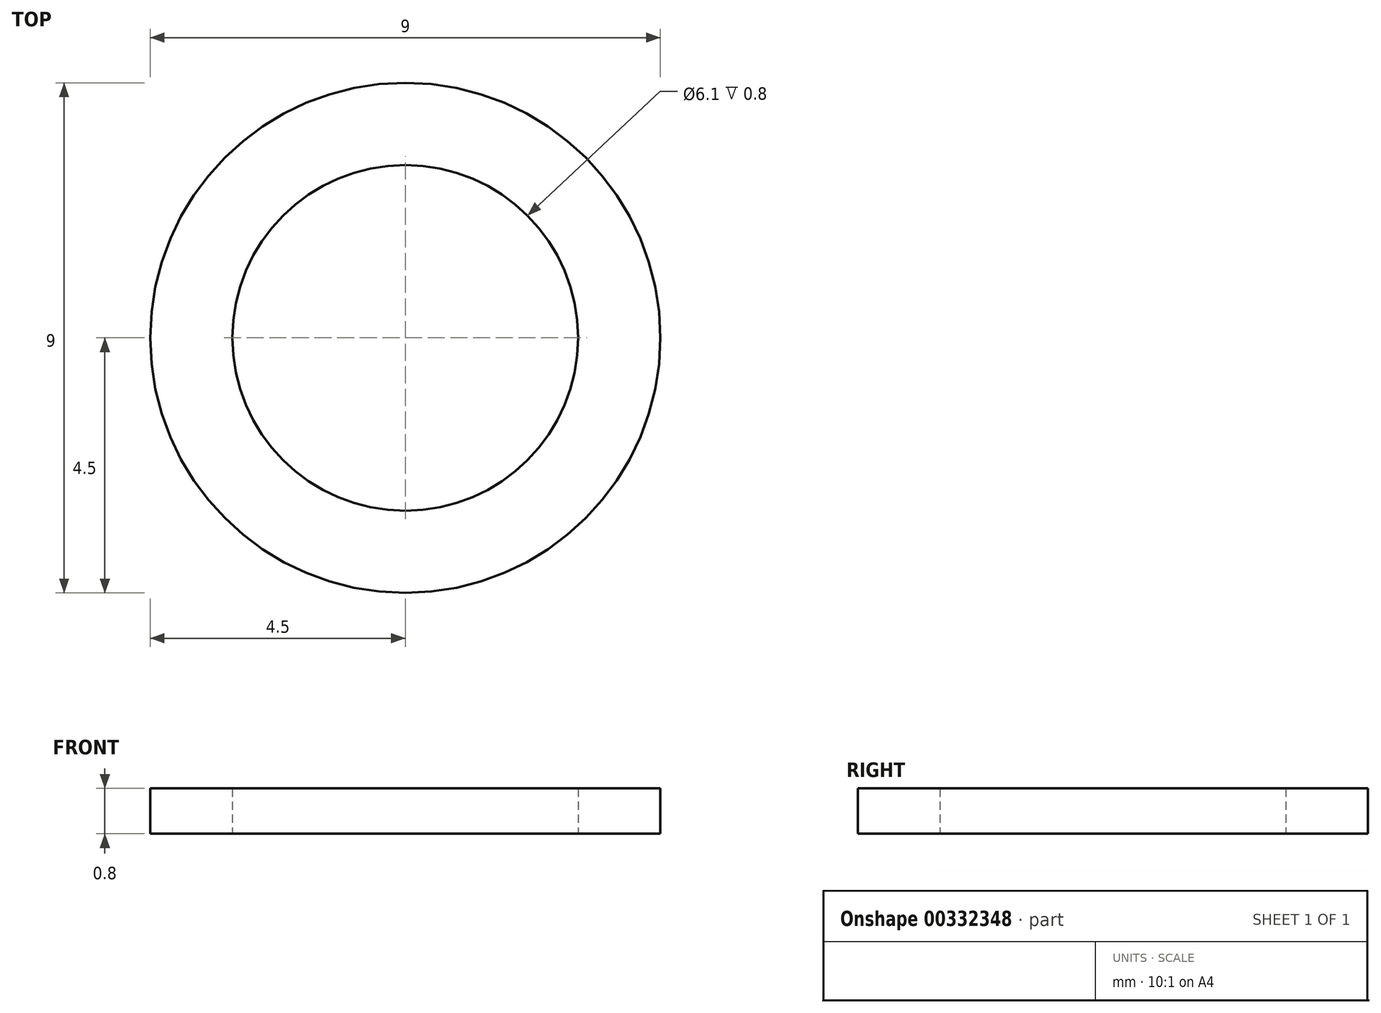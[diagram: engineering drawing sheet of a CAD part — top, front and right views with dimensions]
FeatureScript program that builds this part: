
annotation { "Feature Type Name" : "Feature", "Feature Type Description" : "" }
export const myFeature = defineFeature(function(context is Context, id is Id, definition is map)
    precondition{}
    {
        {
            var Q0;
            Q0=qCreatedBy(makeId("Top.planeOp"),FACE);
            var sketch = newSketch(context, id + "F0", { "sketchPlane" : qUnion([Q0])});
            skCircle(sketch, "E0", {"center": v(0, 0) * mm, "radius": 3.05 * mm});
            skCircle(sketch, "E1", {"center": v(0, 0) * mm, "radius": 4.5 * mm});
            skSolve(sketch);
        }
        {
            var Q0;
            Q0=makeQuery(id+"F0.imprint","IMPRINT",FACE,{"disambiguationData":[TD([[makeQuery(id+"F0.imprint","IMPRINT",EDGE,{"derivedFrom":sQuery(id+"F0.wireOp",EDGE,"E0")}),-1.0]])]});
            extrude(context, id + "F1", {"entities" : qUnion([Q0]), "depth" : 0.8 * mm, "offsetDistance" : 25 * mm});
        }
    });
